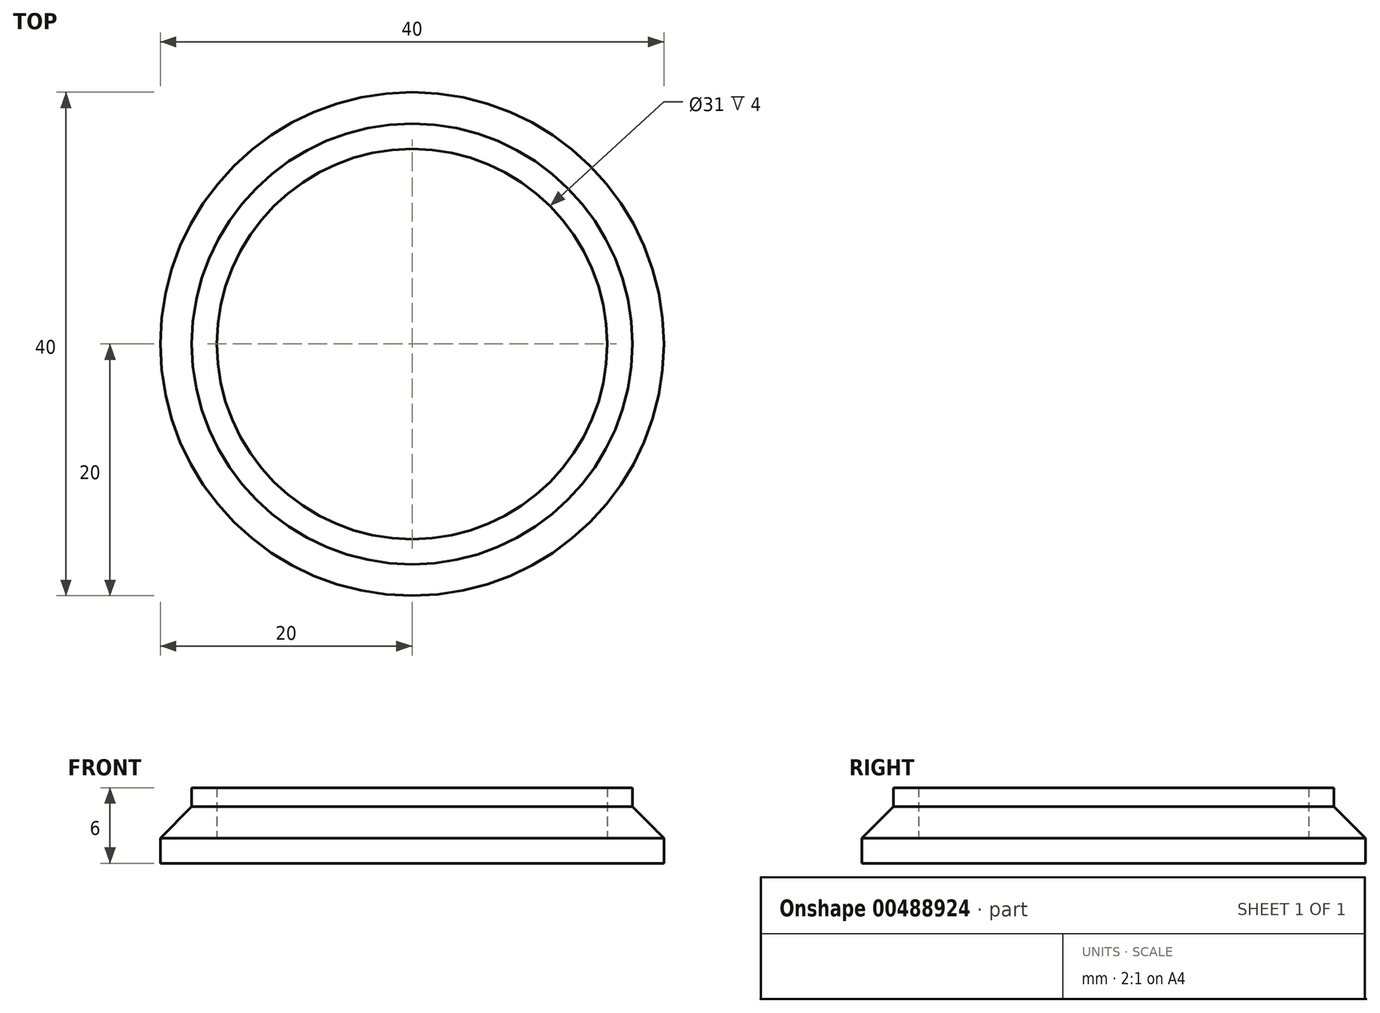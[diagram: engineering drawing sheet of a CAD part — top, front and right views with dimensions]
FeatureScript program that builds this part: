
annotation { "Feature Type Name" : "Feature", "Feature Type Description" : "" }
export const myFeature = defineFeature(function(context is Context, id is Id, definition is map)
    precondition{}
    {
        {
            var Q0;
            Q0=qCreatedBy(makeId("Top.planeOp"),FACE);
            var sketch = newSketch(context, id + "F0", { "sketchPlane" : qUnion([Q0])});
            skCircle(sketch, "E0", {"center": v(0, 0) * mm, "radius": 15.5 * mm});
            skCircle(sketch, "E1", {"center": v(0, 0) * mm, "radius": 17.5 * mm});
            skSolve(sketch);
        }
        {
            var Q0;
            Q0=makeQuery(id+"F0.imprint","IMPRINT",FACE,{"disambiguationData":[TD([[makeQuery(id+"F0.imprint","IMPRINT",EDGE,{"derivedFrom":sQuery(id+"F0.wireOp",EDGE,"E0")}),-1.0]])]});
            extrude(context, id + "F1", {"entities" : qUnion([Q0]), "depth" : 6 * mm});
        }
        {
            var Q0;
            Q0=qCreatedBy(makeId("Top.planeOp"),FACE);
            var sketch = newSketch(context, id + "F2", { "sketchPlane" : qUnion([Q0])});
            skCircle(sketch, "E2", {"center": v(0, 0) * mm, "radius": 20 * mm});
            skSolve(sketch);
        }
        {
            var Q0;
            Q0=makeQuery(id+"F2.imprint","IMPRINT",FACE,{"disambiguationData":[TD([[makeQuery(id+"F2.imprint","IMPRINT",EDGE,{"derivedFrom":sQuery(id+"F2.wireOp",EDGE,"E2")}),1.0]])]});
            extrude(context, id + "F3", {"entities" : qUnion([Q0]), "operationType" : NewBodyOperationType.ADD, "depth" : 2 * mm});
        }
        {
            var Q0;
            Q0=makeQuery(id+"F3.boolean.opBoolean","INTERSECT",EDGE,{"derivedFrom":[makeQuery(id+"F1.opExtrude","SWEPT_FACE",FACE,{"disambiguationData":[OSD([sQuery(id+"F0.wireOp",EDGE,"E1")])]}),makeQuery(id+"F3.opExtrude","CAP_FACE",FACE,{"disambiguationData":[OSD([sQuery(id+"F2.wireOp",EDGE,"E2")])],"isStart":false})]});
            chamfer(context, id + "F4", {"entities" : qUnion([Q0]), "width" : 2.5 * mm, "tangentPropagation" : true});
        }
    });
